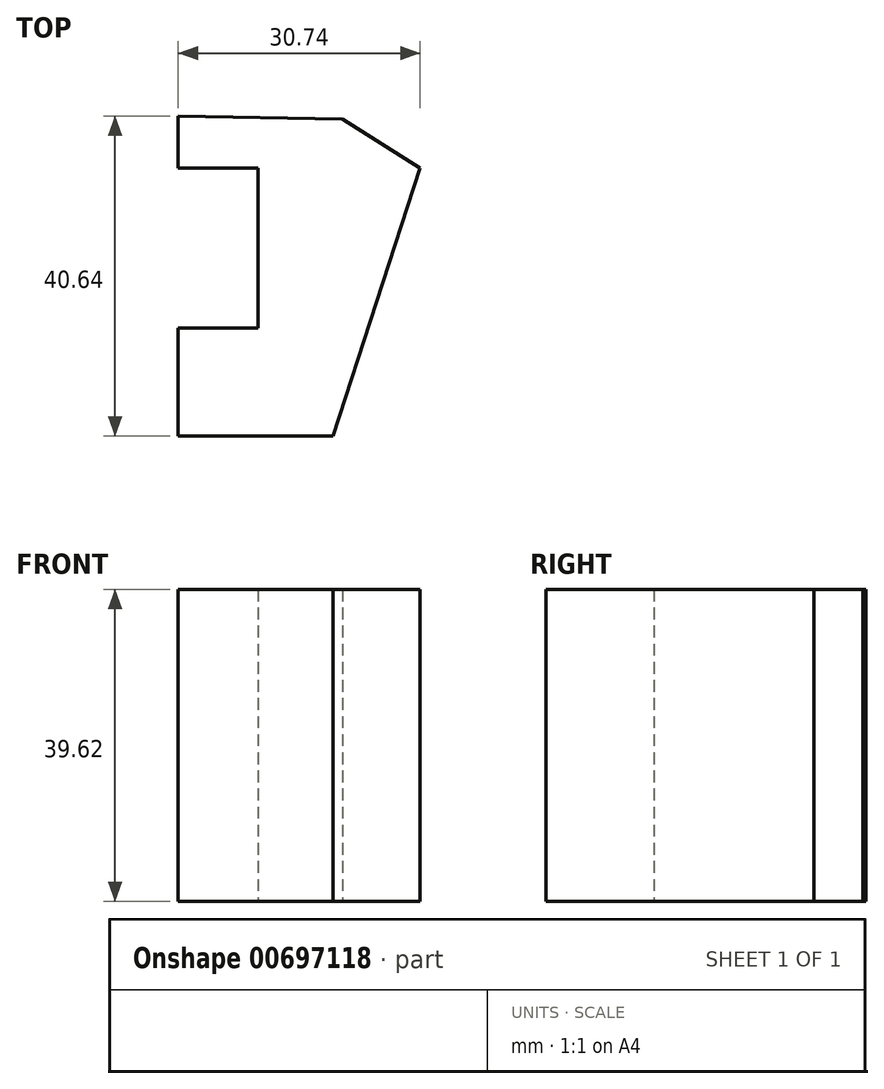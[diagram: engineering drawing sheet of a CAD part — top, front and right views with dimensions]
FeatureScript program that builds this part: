
annotation { "Feature Type Name" : "Feature", "Feature Type Description" : "" }
export const myFeature = defineFeature(function(context is Context, id is Id, definition is map)
    precondition{}
    {
        {
            var Q0;
            Q0=qCreatedBy(makeId("Top.planeOp"),FACE);
            var sketch = newSketch(context, id + "F0", { "sketchPlane" : qUnion([Q0])});
            skLineSegment(sketch, "E0", {"start": v(-10.68, 19.01) * mm, "end": v(-10.68, 12.41) * mm});
            skLineSegment(sketch, "E1", {"start": v(-10.68, 12.41) * mm, "end": v(-0.52, 12.41) * mm});
            skLineSegment(sketch, "E2", {"start": v(-0.52, 12.41) * mm, "end": v(-0.52, -7.9) * mm});
            skLineSegment(sketch, "E3", {"start": v(-0.52, -7.9) * mm, "end": v(-10.68, -7.9) * mm});
            skLineSegment(sketch, "E4", {"start": v(-10.68, -7.9) * mm, "end": v(-10.68, -21.63) * mm});
            skLineSegment(sketch, "E5", {"start": v(-10.68, -21.63) * mm, "end": v(9, -21.63) * mm});
            skLineSegment(sketch, "E6", {"start": v(9, -21.63) * mm, "end": v(20.06, 12.41) * mm});
            skLineSegment(sketch, "E7", {"start": v(20.06, 12.41) * mm, "end": v(10.17, 18.62) * mm});
            skLineSegment(sketch, "E8", {"start": v(10.17, 18.62) * mm, "end": v(-10.68, 19.01) * mm});
            skPoint(sketch, "E9", {"position": v(13.45, -7.9) * mm});
            skSolve(sketch);
        }
        {
            var Q0;
            Q0=makeQuery(id+"F0.imprint","IMPRINT",FACE,{"disambiguationData":[TD([[makeQuery(id+"F0.imprint","IMPRINT",EDGE,{"derivedFrom":sQuery(id+"F0.wireOp",EDGE,"E0")}),1.0]])]});
            extrude(context, id + "F1", {"entities" : qUnion([Q0]), "depth" : 39.62 * mm, "offsetDistance" : 25.4 * mm});
        }
    });
